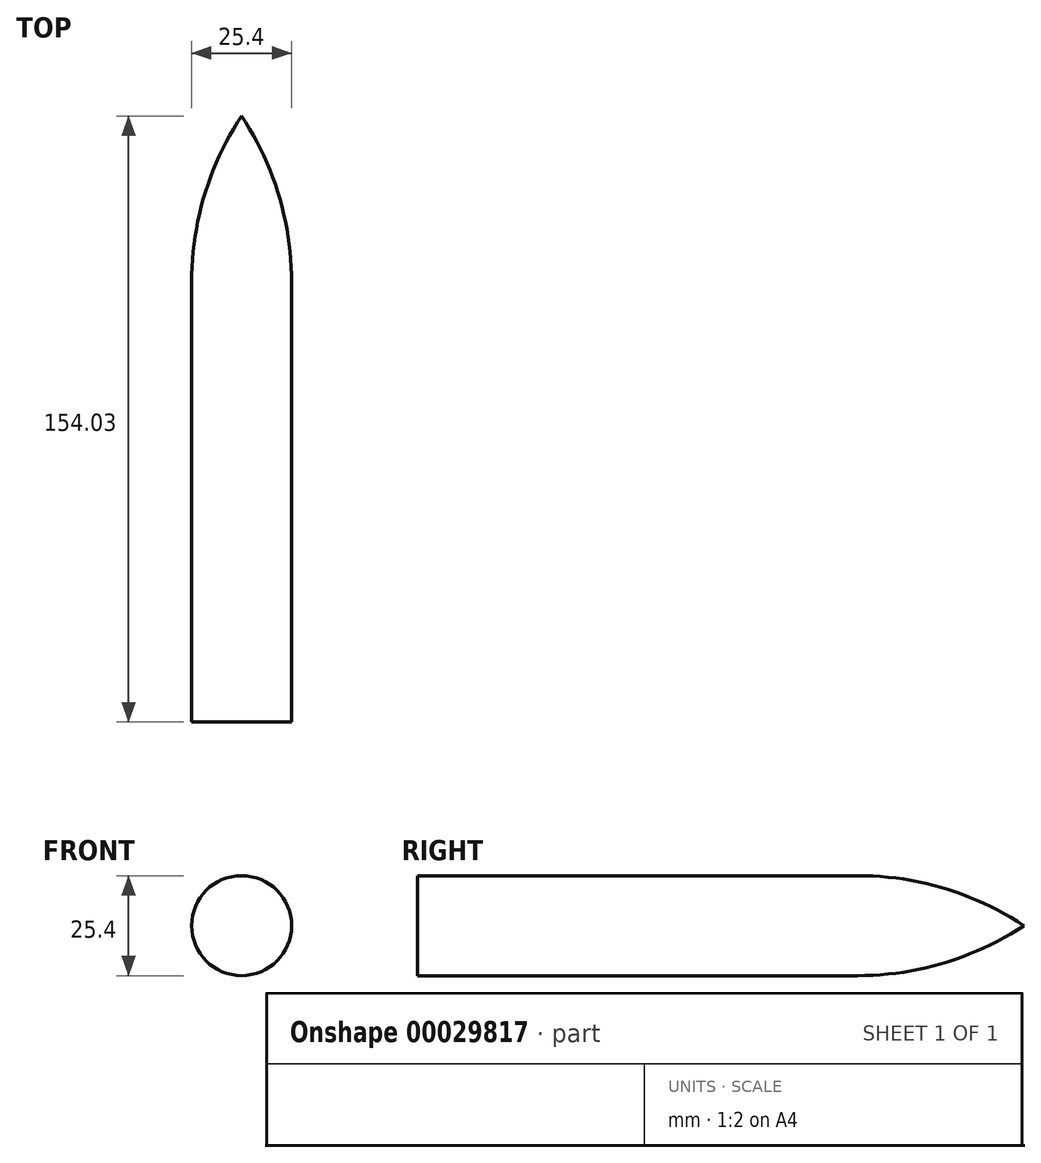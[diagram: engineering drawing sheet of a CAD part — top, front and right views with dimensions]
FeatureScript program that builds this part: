
annotation { "Feature Type Name" : "Feature", "Feature Type Description" : "" }
export const myFeature = defineFeature(function(context is Context, id is Id, definition is map)
    precondition{}
    {
        {
            var Q0;
            Q0=qCreatedBy(makeId("Top.planeOp"),FACE);
            var sketch = newSketch(context, id + "F0", { "sketchPlane" : qUnion([Q0])});
            skLineSegment(sketch, "E0.right", {"start": v(12.7, 0) * mm, "end": v(12.7, 56.13) * mm});
            skLineSegment(sketch, "E1.top", {"start": v(6.35, -55.64) * mm, "end": v(12.7, -55.64) * mm});
            skLineSegment(sketch, "E1.right", {"start": v(12.7, 0) * mm, "end": v(12.7, -55.64) * mm});
            skLineSegment(sketch, "E2", {"start": v(0, 56.13) * mm, "end": v(0, 98.39) * mm});
            skLineSegment(sketch, "E3", {"start": v(0, 98.39) * mm, "end": v(0, 56.13) * mm});
            skArc(sketch, "E4", {"start": v(12.7, 56.13) * mm, "mid": v(9.46, 78.2) * mm, "end": v(0, 98.39) * mm});
            skPoint(sketch, "E5.end.orphan", {"position": v(12.7, 0) * mm});
            skPoint(sketch, "E6.orphan", {"position": v(0, -55.64) * mm});
            skLineSegment(sketch, "E7", {"start": v(0, 56.13) * mm, "end": v(0, -55.64) * mm});
            skLineSegment(sketch, "E8", {"start": v(6.35, -55.64) * mm, "end": v(0, -55.64) * mm});
            skSolve(sketch);
        }
        {
            var Q0;
            Q0=makeQuery(id+"F0.imprint","IMPRINT",FACE,{"disambiguationData":[TD([[makeQuery(id+"F0.imprint","IMPRINT",EDGE,{"derivedFrom":sQuery(id+"F0.wireOp",EDGE,"E0.right")}),1.0]])]});
            var Q1;
            Q1=sQuery(id+"F0.wireOp",EDGE,"E3");
            revolve(context, id + "F1", {"entities" : qUnion([Q0]), "axis" : qUnion([Q1]), "revolveType" : RevolveType.FULL});
        }
    });
